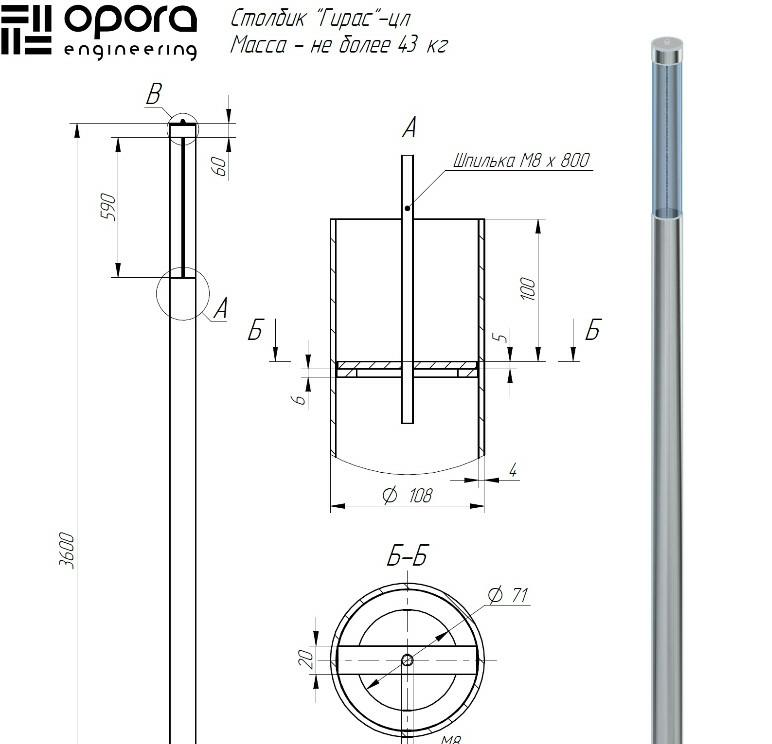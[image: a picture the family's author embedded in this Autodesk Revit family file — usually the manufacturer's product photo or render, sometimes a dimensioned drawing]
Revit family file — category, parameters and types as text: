
# Revit family: Комплект Ферал
name_source: partatom
category: Осветительные приборы
revit_build: Autodesk Revit 2018 (Build: 20180423_1000(x64)
units: mm (PartAtom-declared; Revit-internal decimal feet)

## family parameters
Источник света = Да
Общий = Нет
Основа = Грань
При загрузке вырезать с полостями = Нет
Размер круглого соединителя = Использовать диаметр
Тип детали = Нормальный
Точка расчета площади = Нет

## types (2) — shared parameters
ADSK_Версия Revit = 2018
ADSK_Версия семейства = 1.01
ADSK_Единица измерения = шт.
ADSK_Завод-изготовитель = ООО «ОПОРА ИНЖИНИРИНГ»
ADSK_Классификация нагрузок = Освещение
ADSK_Количество = 1
ADSK_Количество фаз = 1
ADSK_Коэффициент мощности = 0.95
ADSK_Масса = 98.5
ADSK_Масса_Текст = 98.5
ADSK_Материал = Сталь
ADSK_Напряжение = 230 В
ADSK_Номинальная мощность = 55 Вт
ADSK_Обозначение = ГОСТ Р 1.4 – 2004, ГОСТ Р 1.5 – 2004, ГОСТ 16350-80, ГОСТ Р 1.12 – 2004, ГОСТ 8732-78, ГОСТ 10704-81, ГОСТ 11533-75, ГОСТ 27772-88*, ГОСТ 14771 -76, ГОСТ 23518-79, ГОСТ 14776-79*, ГОСТ 9.032-74* ЕСЗК, ГОСТ 9.307-89 ЕСЗК, ГОСТ 23118-99, ГОСТ 24297-87, ГОСТ 15.309-98, ГОСТ Р 15.201-2002
ADSK_Полная мощность = 58 Вт
ADSK_Размер_Длина = 250 мм
ADSK_Размер_Ширина = 250 мм
ADSK_Ток = 0 А
ADSK_Энергоэффективность = 98 лм/Вт
B = 450 мм
Dв = 108 мм
Dн = 159 мм
IK = 08
IP = 65
URL = https://opora-e.com
h1 = 1500 мм
Вид опоры = НФ
Возможный угол наклона = 0
Г = 97 мм
Группа модели = Опоры
Диапазон цветовой температуры = 2700-4000
Изготовитель = ООО «ОПОРА ИНЖИНИРИНГ»
Излучение по ширине линии = 610 мм
Класс Защиты = 1
Класс защиты от поражения электрическим током = I
Класс светораспределения = рассеяный
Климатическая зона = III
Климатическое исполнение = У1
Коэффициент пульсации = не более 5%
Максимальный вес оборудования = 19
Материал рассеивателя = Ударопрочный поликарбонат
Наличие лючка = Да
Область использования = Уличное освещение
Описание = Опоры данной серии предназначены для освещения любых объектов с установкой кронштейнов с большим
количеством светильников, для подвеса проводов СИП и установки рекламных и иных конструкций. Опоры
удовлетворяют требованиям прочности при воздействии нормированной боковой статической нагрузки.
Отметка по умолчанию = 1219 мм
Покрытие = Защитное горячее оцинкование (Ц)
Провод питания = Подземный
Сайт изготовителя = https://www.opora-e.com
Световая отдача = 85
Светофильтр = 16777215
Серия = Опоры несиловые фланцевые (Тип НФ)
Смещение цветовой температуры при затухании лампы = <Нет>
Способ установки = Ф
Срок службы = 25 лет
Телефон изготовителя = +7 (495) 785-50-28
Тип КСС = ШОС
Тип источника света = LED
Тип монтажной поверхности = грунт
Тип опоры = Не силовая
Тип продукции = Опоры несиловые фланцевые (Тип НФ)
Тип фиксации опоры к закладной = Болт
Толщина металла опоры = 6 мм
Угол наклона = 90.00°
Файл фотометрической сетки = LED_50 .ies
Характеристика заземления = Болт заземления М10
Цветопередача = 70
zero-valued in all types: Максимальное горизонтальное усилие

## per-type parameters (varying)
| type | ADSK_Код изделия | ADSK_Наименование краткое | H |
| Осветительный комплект-4,0-цл "Ферал" LED-55/727/YW360F в комплекте с закладной | 19700 | 4,0-цл "Ферал" LED-55/727/YW360F | 4000 мм |
| Осветительный комплект-5,0-цл "Ферал" LED-55/727/YW360F в комплекте с закладной | 19701 | 5,0-цл "Ферал" LED-55/727/YW360F | 5000 мм |

note: column(s) folded — value = type name in every type: ADSK_Марка, ADSK_Наименование
